# Revit family: MECON Turbo-Lux 3
name_source: partatom
category: Rohrzubehör
units: mm (PartAtom-declared; Revit-internal decimal feet)

## family parameters
Arbeitsebenenbasiert = Nein
Beim Laden mit Abzugskörper schneiden = Nein
Bemaßung runder Anschluss = Radius verwenden
Gemeinsam genutzt = Nein
Immer vertikal = Ja
OmniClass-Nummer = 23.60.10.17
OmniClass-Titel = Flow Meters
Teiletyp = Ventil - Zerlegung in

## types (25) — shared parameters
Black = Metal - black
Dark Grey = Metal - RAL7024
Delivery Time = in stock
Download Test Certificate = https://download.mecon.de
FM Certificate = https://www.mecon.de
Glass = Glass-
Grey = Metal - grey
Hersteller = MECON GmbH, Röntgenstraße 105, 50169 Kerpen, Germany
IfcExportAs = IfcFlowMeter
IfcExportType = FLOWMETER
Operating Manual = https://www.mecon.de
Technical Data Sheet = https://www.mecon.de
URL = https://www.mecon.de
Website Product = https://www.mecon.de
iFM = Ja
zero-valued in all types: Vorgabe-Ansicht

## per-type parameters (varying)
| type | Approval | Build in Length | Flow Range | LPCB Certificate | Modell | Nominal_Diameter | Nominal_Radius | Order Code | Typenkommentare | VdS Approval | iD2 | iLPCB | iR1 | iVdS |
| 6"/ DN 150, 1000 USgpm (ø165.1 mm) | FM, LPCB,VdS | 200 mm  [stored 0.656168 ft] | 1500 - 7500 l/min / 400 - 2000 USgpm | https://www.mecon.de | 6"/ DN  150 for pump rate 1000 gpm (ø 165,1 mm) with FM, LPCB and VdS approval | 150 mm | 75 mm | 7ME5835-0AA00-0XM0 | 6"/ DN  150, 1000 gpm (ø165.1 mm) FM/LPCP/VdS | https://www.mecon.de | 165 mm  [stored 0.541339 ft] | Ja | 79 mm | Ja |
| 6"/ DN 150, 750 USgpm (ø165.1 mm) | FM, LPCB,VdS | 200 mm  [stored 0.656168 ft] | 1130 - 5650 l/min / 300 - 1500 USgpm | https://www.mecon.de | 6"/ DN  150 for pump rate 750 gpm (ø 165,1 mm) with FM, LPCB and VdS approval | 150 mm | 75 mm | 7ME5835-0AA00-0XL0 | 6"/ DN  150, 750 gpm (ø165.1 mm) FM/LPCP/VdS | https://www.mecon.de | 165 mm  [stored 0.541339 ft] | Ja | 79 mm | Ja |
| 6"/ DN 150, 500 USgpm (ø165.1 mm) | FM, LPCB,VdS | 200 mm  [stored 0.656168 ft] | 760 - 3800 l/min / 200 - 1000 USgpm | https://www.mecon.de | 6"/ DN  150 for pump rate 500 gpm (ø 165,1 mm) with FM, LPCB and VdS approval | 150 mm | 75 mm | 7ME5835-0AA00-0XK0 | 6"/ DN  150, 500 gpm (ø165.1 mm) FM/LPCP/VdS | https://www.mecon.de | 165 mm  [stored 0.541339 ft] | Ja | 79 mm | Ja |
| 6"/ DN 150, 1000 USgpm (ø168.3 mm) | FM, LPCB,VdS | 200 mm  [stored 0.656168 ft] | 1500 - 7500 l/min / 400 - 2000 USgpm | https://www.mecon.de | 6"/ DN  150 for pump rate 1000 gpm (ø 168,3 mm) with FM, LPCB and VdS approval | 150 mm | 75 mm | 7ME5835-0AA00-0KM0 | 6"/ DN  150, 1000 gpm (ø168.3 mm) FM/LPCP/VdS | https://www.mecon.de | 165 mm  [stored 0.541339 ft] | Ja | 79 mm | Ja |
| 6"/ DN 150, 750 USgpm (ø168.3 mm) | FM, LPCB,VdS | 200 mm  [stored 0.656168 ft] | 1130 - 5650 l/min / 300 - 1500 USgpm | https://www.mecon.de | 6"/ DN  150 for pump rate 750 gpm (ø 168,3 mm) with FM, LPCB and VdS approval | 150 mm | 75 mm | 7ME5835-0AA00-0KL0 | 6"/ DN  150, 750 gpm (ø168.3 mm) FM/LPCP/VdS | https://www.mecon.de | 165 mm  [stored 0.541339 ft] | Ja | 79 mm | Ja |
| 6"/ DN 150, 500 USgpm (ø168.3 mm) | FM, LPCB,VdS | 200 mm  [stored 0.656168 ft] | 760 - 3800 l/min / 200 - 1000 USgpm | https://www.mecon.de | 6"/ DN  150 for pump rate 500 gpm (ø 168,3 mm) with FM, LPCB and VdS approval | 150 mm | 75 mm | 7ME5835-0AA00-0KK0 | 6"/ DN  150, 500 gpm (ø168.3 mm) FM/LPCP/VdS | https://www.mecon.de | 165 mm  [stored 0.541339 ft] | Ja | 79 mm | Ja |
| 4"/ DN 100, 450 USgpm (ø114.3 mm) | FM, LPCB,VdS | 100 mm  [stored 0.328084 ft] | 680 - 3400 l/min / 180 - 900 USgpm | https://www.mecon.de | 4"/ DN  100 for pump rate 450 gpm (ø 114,3 mm) with FM, LPCB and VdS approval | 100 mm | 50 mm | 7ME5835-0AA00-0HJ0 | 4"/ DN  100, 450 gpm (ø114.3 mm) FM/LPCP/VdS | https://www.mecon.de | 140 mm  [stored 0.459318 ft] | Ja | 54 mm | Ja |
| 4"/ DN 100, 400 USgpm (ø114.3 mm) | FM, LPCB,VdS | 100 mm  [stored 0.328084 ft] | 600 - 3000 l/min / 160 - 800 USgpm | https://www.mecon.de | 4"/ DN  100 for pump rate 400 gpm (ø 114,3 mm) with FM, LPCB und VdS approval | 100 mm | 50 mm | 7ME5835-0AA00-0HH0 | 4"/ DN  100, 400 gpm (ø114.3 mm) FM/LPCP/VdS | https://www.mecon.de | 140 mm  [stored 0.459318 ft] | Ja | 54 mm | Ja |
| 4"/ DN 100, 300 USgpm (ø114.3 mm) | FM, LPCB,VdS | 100 mm  [stored 0.328084 ft] | 460 - 2300 l/min / 120 - 600 USgpm | https://www.mecon.de | 4"/ DN  100 for pump rate 300 gpm (ø 114,3 mm) with FM, LPCB and VdS approval | 100 mm | 50 mm | 7ME5835-0AA00-0HG0 | 4"/ DN  100, 300 gpm (ø114.3 mm) FM/LPCP/VdS | https://www.mecon.de | 140 mm  [stored 0.459318 ft] | Ja | 54 mm | Ja |
| 3"/ DN 80, 200 USgpm (ø88.9 mm) | FM, LPCB,VdS | 100 mm  [stored 0.328084 ft] | 300 - 1500 l/min / 80 - 400 USgpm | https://www.mecon.de | 3"/ DN 80 for pump rate 200 gpm (ø 88,9 mm) with FM, LPCB and VdS approval | 80 mm | 40 mm | 7ME5835-0AA00-0GE0 | 3"/ DN 80 200 gpm (ø88.9 mm) FM/LPCP/VdS | https://www.mecon.de | 130 mm  [stored 0.426509 ft] | Ja | 44 mm  [stored 0.144357 ft] | Ja |
| 3"/ DN 80, 150 USgpm (ø88.9 mm) | FM, LPCB,VdS | 100 mm  [stored 0.328084 ft] | 220 - 1100 l/min / 60 - 300 USgpm | https://www.mecon.de | 3"/ DN 80 for pump rate 150 gpm (ø 88,9 mm) with FM, LPCB and VdS approval | 80 mm | 40 mm | 7ME5835-0AA00-0GD0 | 3"/ DN 80, 150 gpm (ø88.9 mm) FM/LPCP/VdS | https://www.mecon.de | 130 mm  [stored 0.426509 ft] | Ja | 44 mm  [stored 0.144357 ft] | Ja |
| 2½"/ DN 65, 100 USgpm (ø73.0 mm) | FM | 100 mm  [stored 0.328084 ft] | 150 - 750 l/min / 40 - 200 USgpm |  | 2½"/ DN 65 for pump rate 100 gpm (ø 73,0 mm) with FM approval | 65 mm | 33 mm | 7ME5835-0AA00-0UC0 | 2½"/ DN 65, 100 gpm (ø73.0 mm) FM |  | 122.5 mm  [stored 0.401903 ft] | Nein | 36.5 mm  [stored 0.119751 ft] | Nein |
| 2½"/ DN 65, 100 USgpm (ø76.1 mm) | FM, LPCB,VdS | 100 mm  [stored 0.328084 ft] | 150 - 750 l/min / 40 - 200 USgpm | https://www.mecon.de | 2½"/ DN 65 for pump rate 100 gpm (ø 76,1 mm)  with FM, LPCB and VdS approval | 65 mm | 33 mm | 7ME5835-0AA00-0FC0 | 2½"/ DN 65, 100 gpm (ø76.1 mm)  FM/LPCP/VdS | https://www.mecon.de | 122.5 mm  [stored 0.401903 ft] | Ja | 36.5 mm  [stored 0.119751 ft] | Ja |
| 2"/ DN 50, 50 USgpm (ø60.3 mm) | FM, LPCB,VdS | 100 mm  [stored 0.328084 ft] | 75 - 375 l/min / 20 - 100 USgpm | https://www.mecon.de | 2"/ DN 50 for pump rate 50 gpm (ø 60,3 mm) with FM, LPCB and VdS approval | 50 mm | 25 mm | 7ME5835-0AA00-0EB0 | 2"/ DN 50, 50 gpm (ø60.3 mm) FM/LPCP/VdS | https://www.mecon.de | 115 mm  [stored 0.377297 ft] | Ja | 29 mm  [stored 0.0951444 ft] | Ja |
| 4"/ DN 100, 250 USgpm (ø114.3 mm) | FM, LPCB,VdS | 100 mm  [stored 0.328084 ft] | 380 - 1900 l/min / 100 - 500 USgpm | https://www.mecon.de | 4"/ DN  100 for pump rate 250 gpm (ø 114,3 mm) with FM, LPCB and VdS approval | 100 mm | 50 mm | 7ME5835-0AA00-0HF0 | 4" / DN 100, 250 gpm (ø114.3 mm) FM/LPCP/VdS | https://www.mecon.de | 140 mm  [stored 0.459318 ft] | Ja | 54 mm | Ja |
| 6"/ DN 150, 1250 USgpm (ø168.3 mm) | FM, LPCB,VdS | 200 mm  [stored 0.656168 ft] | 1900 - 9500 l/min / 500 - 2500 USgpm | https://www.mecon.de | 6"/ DN  150 for pump rate 1250 gpm (ø 168,3 mm) with FM, LPCB and VdS approval | 150 mm | 75 mm | 7ME5835-0AA00-0KN0 | 6"/ DN  150, 1250 gpm (ø168.3 mm) FM/LPCP/VdS | https://www.mecon.de | 165 mm  [stored 0.541339 ft] | Ja | 79 mm | Ja |
| 6"/ DN 150, 1250 USgpm (ø165.1 mm) | FM, LPCB,VdS | 200 mm  [stored 0.656168 ft] | 1900 - 9500 l/min / 500 - 2500 USgpm | https://www.mecon.de | 6"/ DN  150 for pump rate 1250 gpm (ø 165,1 mm) with FM, LPCB and VdS approval | 150 mm | 75 mm | 7ME5835-0AA00-0XN0 | 6"/ DN  150, 1250 gpm (ø165.1 mm) FM/LPCP/VdS | https://www.mecon.de | 165 mm  [stored 0.541339 ft] | Ja | 79 mm | Ja |
| 8"/ DN 200, 1500 USgpm (ø219.1 mm) | FM, LPCB,VdS | 200 mm  [stored 0.656168 ft] | 2200 - 11000 l/min / 600 - 3000 USgpm | https://www.mecon.de | 8"/ DN  200 for pump rate 1500 gpm (ø 219,1 mm) with FM, LPCB and VdS approval | 200 mm | 100 mm | 7ME5835-0AA00-0LP0 | 8"/ DN  200, 1500 gpm (ø219.1 mm) FM/LPCP/VdS | https://www.mecon.de | 190 mm  [stored 0.62336 ft] | Ja | 104 mm | Ja |
| 8"/ DN 200, 2000 USgpm (ø219.1 mm) | FM, LPCB,VdS | 200 mm  [stored 0.656168 ft] | 3000 - 15000 l/min / 800 - 4000 USgpm | https://www.mecon.de | 8"/ DN  200 for pump rate 2000 gpm (ø 219,1 mm) with FM, LPCB and VdS approval | 200 mm | 100 mm | 7ME5835-0AA00-0LQ0 | 8"/ DN  200, 2000 gpm (ø219.1 mm) FM/LPCP/VdS | https://www.mecon.de | 190 mm  [stored 0.62336 ft] | Ja | 104 mm | Ja |
| 8"/ DN 200, 2500 USgpm (ø219.1 mm) | FM, LPCB,VdS | 200 mm  [stored 0.656168 ft] | 3800 - 19000 l/min / 1000 - 5000 USgpm | https://www.mecon.de | 8"/ DN  200 for pump rate 2500 gpm (ø 219,1 mm) with FM, LPCB and VdS approval | 200 mm | 100 mm | 7ME5835-0AA00-0LR0 | 8"/ DN  200, 2500 gpm (ø219.1 mm) FM/LPCP/VdS | https://www.mecon.de | 190 mm  [stored 0.62336 ft] | Ja | 104 mm | Ja |
| 8"/ DN 200, 3000 USgpm (ø219.1 mm) | FM, LPCB,VdS | 200 mm  [stored 0.656168 ft] | 4500 - 22500 l/min / 1200 - 6000 USgpm | https://www.mecon.de | 8"/ DN  200 for pump rate 3000 gpm (ø 219,1 mm) with FM, LPCB and VdS approval | 200 mm | 100 mm | 7ME5835-0AA00-0LS0 | 8"/ DN  200, 3000 gpm (ø219.1 mm) FM/LPCP/VdS | https://www.mecon.de | 190 mm  [stored 0.62336 ft] | Ja | 104 mm | Ja |
| 10"/ DN 250, 3500 USgpm (ø273.0 mm) | FM | 200 mm  [stored 0.656168 ft] | 5300 - 26500 l/min / 1400 - 7000 USgpm |  | 10"/ DN  250 for pump rate 3500 gpm (ø 273,0 mm) with FM approval | 250 mm | 125 mm | 7ME5835-0AA00-0MT0 | 10"/ DN  250, 3500 gpm (ø273.0 mm) FM |  | 215 mm  [stored 0.705381 ft] | Nein | 129 mm  [stored 0.423228 ft] | Nein |
| 10"/ DN 250, 4000 USgpm (ø273.0 mm) | FM | 200 mm  [stored 0.656168 ft] | 6000 - 30000 l/min / 1600 - 8000 USgpm |  | 10"/ DN  250 for pump rate 4000 gpm (ø 273,0 mm) with FM approval | 250 mm | 125 mm | 7ME5835-0AA00-0MU0 | 10"/ DN  250, 4000 gpm (ø273.0 mm) FM |  | 215 mm  [stored 0.705381 ft] | Nein | 129 mm  [stored 0.423228 ft] | Nein |
| 10"/ DN 250, 4500 USgpm (ø273.0 mm) | FM | 200 mm  [stored 0.656168 ft] | 6800 - 34000 l/min / 1800 - 9000 USgpm |  | 10"/ DN  250 for pump rate 4500 gpm (ø 273,0 mm) with FM approval | 250 mm | 125 mm | 7ME5835-0AA00-0MV0 | 10"/ DN  250, 4500 gpm (ø273.0 mm) FM |  | 215 mm  [stored 0.705381 ft] | Nein | 129 mm  [stored 0.423228 ft] | Nein |
| 12"/ DN 300, 5000 USgpm (ø323.9 mm) | FM | 200 mm  [stored 0.656168 ft] | 7600 - 38000 l/min / 2000 - 10000 USgpm |  | 12"/ DN  300 for pump rate 5000 gpm (ø 323,9 mm) with FM approval | 300 mm | 150 mm | 7ME5835-0AA00-0NW0 | 12"/ DN  300, 5000 gpm (ø323.9 mm) FM |  | 240 mm  [stored 0.787402 ft] | Nein | 154 mm  [stored 0.505249 ft] | Nein |

note: [stored X ft] marks values corroborated as IEEE doubles in the binary element streams (Revit-internal decimal feet)
